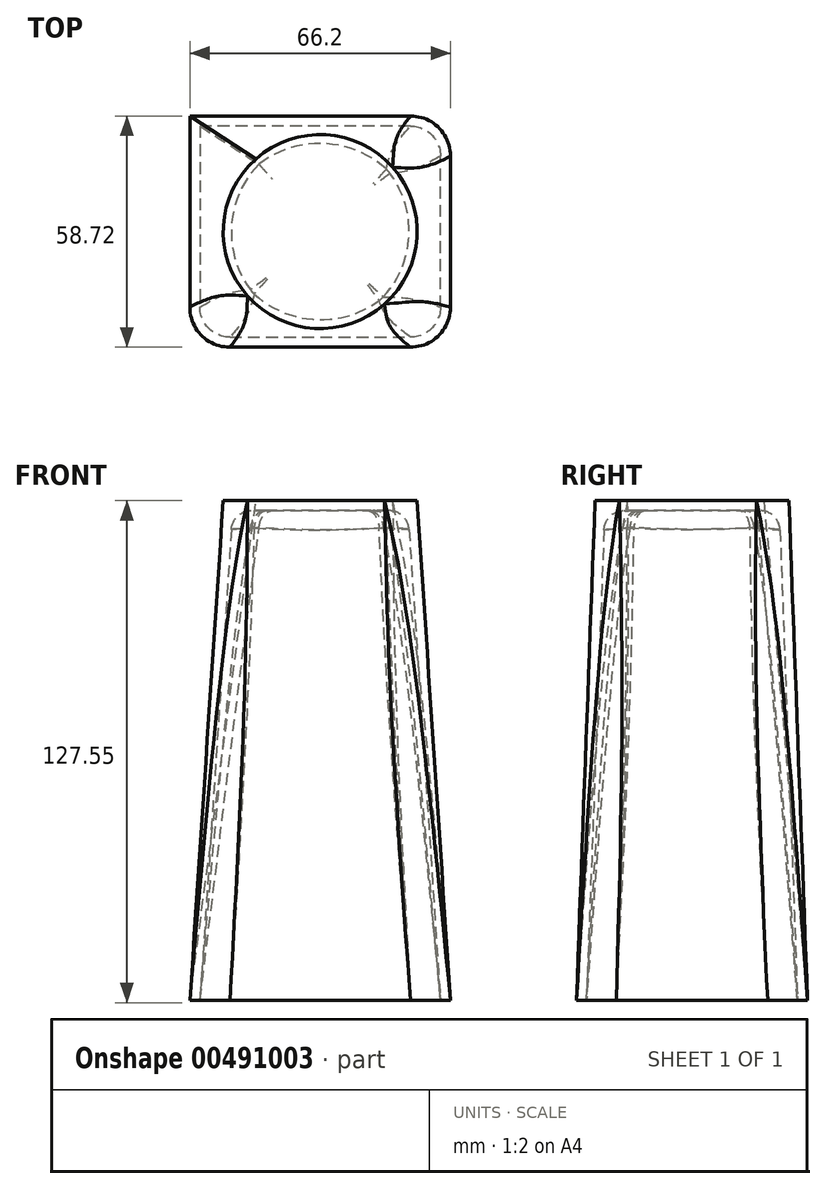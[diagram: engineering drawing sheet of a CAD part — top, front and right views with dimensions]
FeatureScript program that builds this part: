
annotation { "Feature Type Name" : "Feature", "Feature Type Description" : "" }
export const myFeature = defineFeature(function(context is Context, id is Id, definition is map)
    precondition{}
    {
        {
            var Q0;
            Q0=qCreatedBy(makeId("Top.planeOp"),FACE);
            var sketch = newSketch(context, id + "F0", { "sketchPlane" : qUnion([Q0])});
            skLineSegment(sketch, "E0.bottom", {"start": v(33.1, 29.36) * mm, "end": v(-33.1, 29.36) * mm});
            skLineSegment(sketch, "E0.top", {"start": v(33.1, -29.36) * mm, "end": v(-33.1, -29.36) * mm});
            skLineSegment(sketch, "E0.left", {"start": v(33.1, 29.36) * mm, "end": v(33.1, -29.36) * mm});
            skLineSegment(sketch, "E0.right", {"start": v(-33.1, 29.36) * mm, "end": v(-33.1, -29.36) * mm});
            skPoint(sketch, "E0.middle", {"position": v(0, 0) * mm});
            skSolve(sketch);
        }
        {
            var Q0;
            Q0=qCreatedBy(makeId("Top.planeOp"),FACE);
            cPlane(context, id + "F1", {"entities" : qUnion([Q0]), "cplaneType" : CPlaneType.OFFSET, "offset" : 127 * mm, "width" : 152.4 * mm, "height" : 152.4 * mm});
        }
        {
            var Q0;
            Q0=qCreatedBy(id+"F1.planeOp",FACE);
            var sketch = newSketch(context, id + "F2", { "sketchPlane" : qUnion([Q0])});
            skCircle(sketch, "E1", {"center": v(0, 0) * mm, "radius": 24.63 * mm});
            skSolve(sketch);
        }
        {
            var Q0;
            Q0=makeQuery(id+"F0.imprint","IMPRINT",FACE,{"disambiguationData":[TD([[makeQuery(id+"F0.imprint","IMPRINT",EDGE,{"derivedFrom":sQuery(id+"F0.wireOp",EDGE,"E0.bottom")}),1.0]])]});
            var Q1;
            Q1=makeQuery(id+"F2.imprint","IMPRINT",FACE,{"disambiguationData":[TD([[makeQuery(id+"F2.imprint","IMPRINT",EDGE,{"derivedFrom":sQuery(id+"F2.wireOp",EDGE,"E1")}),1.0]])]});
            loft(context, id + "F3", {"sheetProfilesArray" : [{ "sheetProfileEntities" : qUnion([Q0]) }, { "sheetProfileEntities" : qUnion([Q1]) }]});
        }
        {
            var Q0;
            Q0=makeQuery(id+"F3.opLoft","SWEPT_EDGE",EDGE,{"disambiguationData":[OSD([sQuery(id+"F0.wireOp",EDGE,"E0.bottom"),sQuery(id+"F0.wireOp",EDGE,"E0.left")])]});
            var Q1;
            Q1=makeQuery(id+"F3.opLoft","SWEPT_EDGE",EDGE,{"disambiguationData":[OSD([sQuery(id+"F0.wireOp",EDGE,"E0.top"),sQuery(id+"F0.wireOp",EDGE,"E0.left"),sQuery(id+"F0.wireOp",EDGE,"E0.right"),sQuery(id+"F2.wireOp",EDGE,"E1")])]});
            var Q2;
            Q2=makeQuery(id+"F3.opLoft","SWEPT_EDGE",EDGE,{"disambiguationData":[OSD([sQuery(id+"F0.wireOp",EDGE,"E0.bottom"),sQuery(id+"F0.wireOp",EDGE,"E0.top"),sQuery(id+"F0.wireOp",EDGE,"E0.right"),sQuery(id+"F2.wireOp",EDGE,"E1")])]});
            var Q3;
            Q3=makeQuery(id+"F3.opLoft","SWEPT_EDGE",EDGE,{"disambiguationData":[OSD([sQuery(id+"F0.wireOp",EDGE,"E0.bottom"),sQuery(id+"F0.wireOp",EDGE,"E0.left"),sQuery(id+"F0.wireOp",EDGE,"E0.right"),sQuery(id+"F2.wireOp",EDGE,"E1")])]});
            fillet(context, id + "F4", {"entities" : qUnion([Q0, Q1, Q2, Q3]), "radius" : 10.16 * mm, "tangentPropagation" : true, "allowEdgeOverflow" : false});
        }
        {
            var Q0;
            Q0=makeQuery(id+"F3.opLoft","CAP_FACE",FACE,{"disambiguationData":[OSD([makeQuery(id+"F0.imprint","IMPRINT",FACE,{"disambiguationData":[TD([[makeQuery(id+"F0.imprint","IMPRINT",EDGE,{"derivedFrom":sQuery(id+"F0.wireOp",EDGE,"E0.bottom")}),1.0]])]})])],"isStart":true});
            shell(context, id + "F5", {"entities" : qUnion([Q0]), "thickness" : 2.54 * mm});
        }
        {
            var Q0;
            Q0=makeQuery(id+"F5.opShell","OFFSET_FACE",FACE,{"disambiguationData":[OSD([makeQuery(id+"F2.imprint","IMPRINT",FACE,{"disambiguationData":[TD([[makeQuery(id+"F2.imprint","IMPRINT",EDGE,{"derivedFrom":sQuery(id+"F2.wireOp",EDGE,"E1")}),1.0]])]})])]});
            fillet(context, id + "F6", {"entities" : qUnion([Q0]), "radius" : 5.08 * mm, "tangentPropagation" : true, "allowEdgeOverflow" : false});
        }
    });
